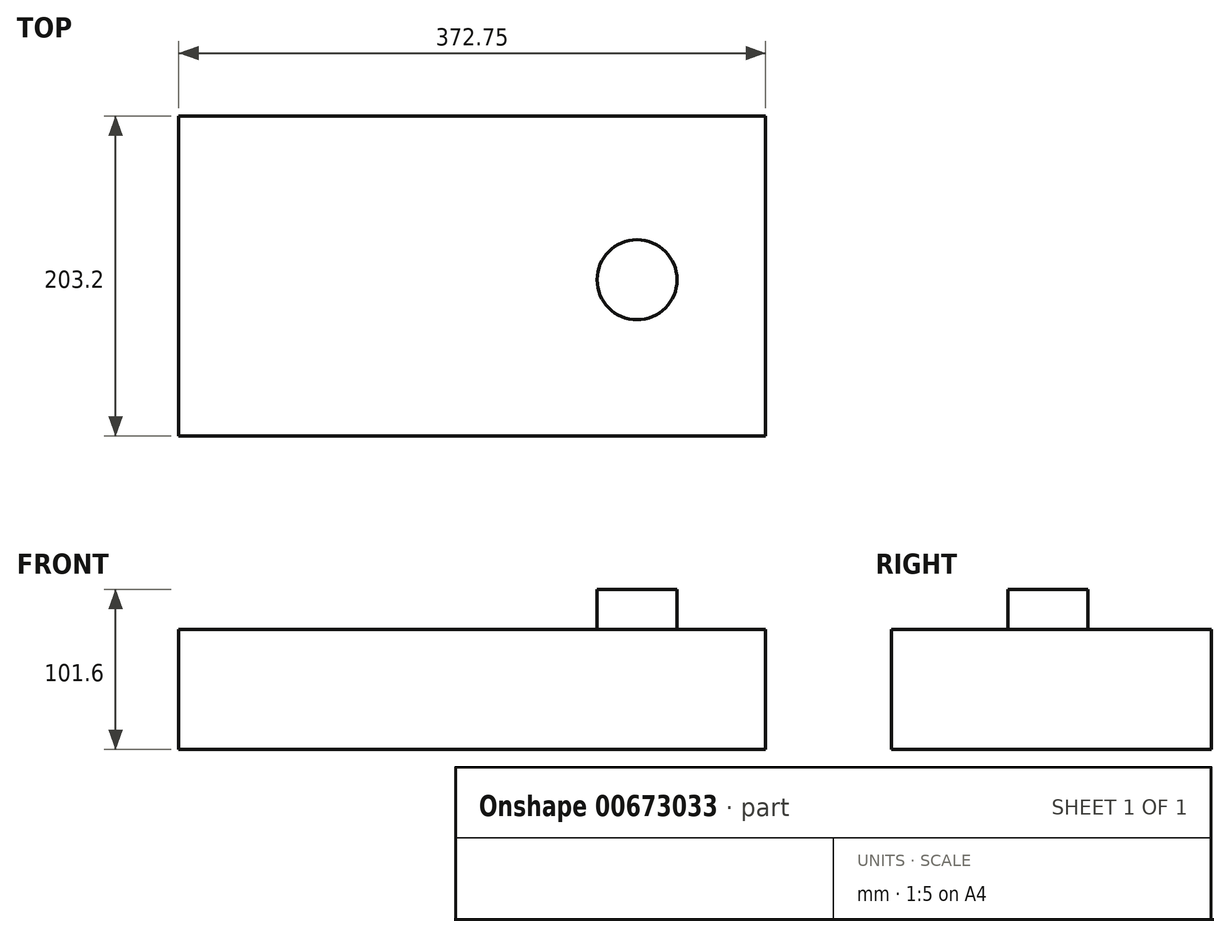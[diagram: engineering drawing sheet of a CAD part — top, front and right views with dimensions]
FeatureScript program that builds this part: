
annotation { "Feature Type Name" : "Feature", "Feature Type Description" : "" }
export const myFeature = defineFeature(function(context is Context, id is Id, definition is map)
    precondition{}
    {
        {
            var Q0;
            Q0=qCreatedBy(makeId("Front.planeOp"),FACE);
            var sketch = newSketch(context, id + "F0", { "sketchPlane" : qUnion([Q0])});
            skLineSegment(sketch, "E0", {"start": v(0, 0) * mm, "end": v(372.75, 0) * mm});
            skLineSegment(sketch, "E1", {"start": v(372.75, 0) * mm, "end": v(372.75, -76.2) * mm});
            skLineSegment(sketch, "E2", {"start": v(372.75, -76.2) * mm, "end": v(0, -76.2) * mm});
            skLineSegment(sketch, "E3", {"start": v(0, -76.2) * mm, "end": v(0, 0) * mm});
            skSolve(sketch);
        }
        {
            var Q0;
            Q0=makeQuery(id+"F0.imprint","IMPRINT",FACE,{"disambiguationData":[TD([[makeQuery(id+"F0.imprint","IMPRINT",EDGE,{"derivedFrom":sQuery(id+"F0.wireOp",EDGE,"E0")}),-1.0]])]});
            extrude(context, id + "F1", {"entities" : qUnion([Q0]), "depth" : 203.2 * mm, "offsetDistance" : 25.4 * mm});
        }
        {
            var Q0;
            Q0=makeQuery(id+"F1.opExtrude","SWEPT_FACE",FACE,{"disambiguationData":[OSD([sQuery(id+"F0.wireOp",EDGE,"E0")])]});
            var sketch = newSketch(context, id + "F2", { "sketchPlane" : qUnion([Q0])});
            skCircle(sketch, "E4", {"center": v(291.12, -103.96) * mm, "radius": 25.4 * mm});
            skSolve(sketch);
        }
        {
            var Q0;
            Q0 = qSketchRegion(id + "F2", true);
            extrude(context, id + "F3", {"entities" : qUnion([Q0]), "operationType" : NewBodyOperationType.ADD, "depth" : 25.4 * mm, "offsetDistance" : 25.4 * mm});
        }
    });
